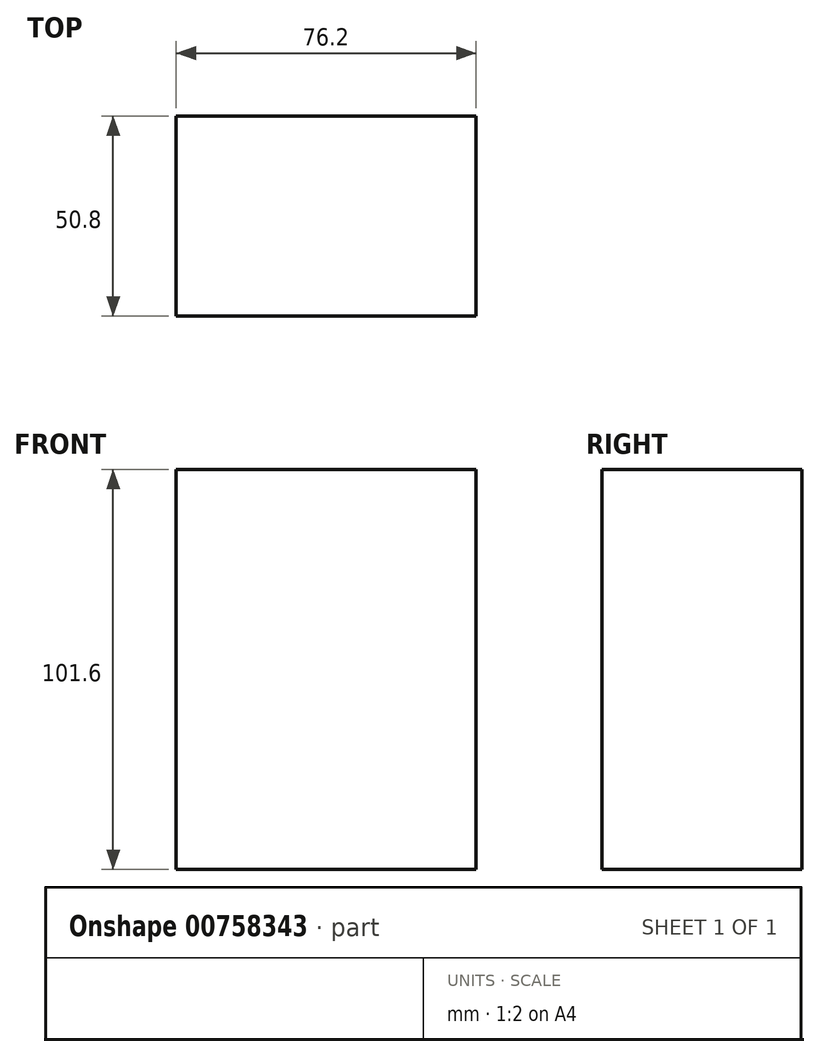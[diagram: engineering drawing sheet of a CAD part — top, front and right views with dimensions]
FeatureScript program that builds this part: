
annotation { "Feature Type Name" : "Feature", "Feature Type Description" : "" }
export const myFeature = defineFeature(function(context is Context, id is Id, definition is map)
    precondition{}
    {
        {
            var Q0;
            Q0=qCreatedBy(makeId("Top.planeOp"),FACE);
            var sketch = newSketch(context, id + "F0", { "sketchPlane" : qUnion([Q0])});
            skLineSegment(sketch, "E0.bottom", {"start": v(38.1, -25.4) * mm, "end": v(-38.1, -25.4) * mm});
            skLineSegment(sketch, "E0.top", {"start": v(38.1, 25.4) * mm, "end": v(-38.1, 25.4) * mm});
            skLineSegment(sketch, "E0.left", {"start": v(38.1, -25.4) * mm, "end": v(38.1, 25.4) * mm});
            skLineSegment(sketch, "E0.right", {"start": v(-38.1, -25.4) * mm, "end": v(-38.1, 25.4) * mm});
            skPoint(sketch, "E0.middle", {"position": v(0, 0) * mm});
            skSolve(sketch);
        }
        {
            var Q0;
            Q0=makeQuery(id+"F0.imprint","IMPRINT",FACE,{"disambiguationData":[TD([[makeQuery(id+"F0.imprint","IMPRINT",EDGE,{"derivedFrom":sQuery(id+"F0.wireOp",EDGE,"E0.bottom")}),-1.0]])]});
            extrude(context, id + "F1", {"entities" : qUnion([Q0]), "depth" : 101.6 * mm, "offsetDistance" : 25.4 * mm});
        }
    });
